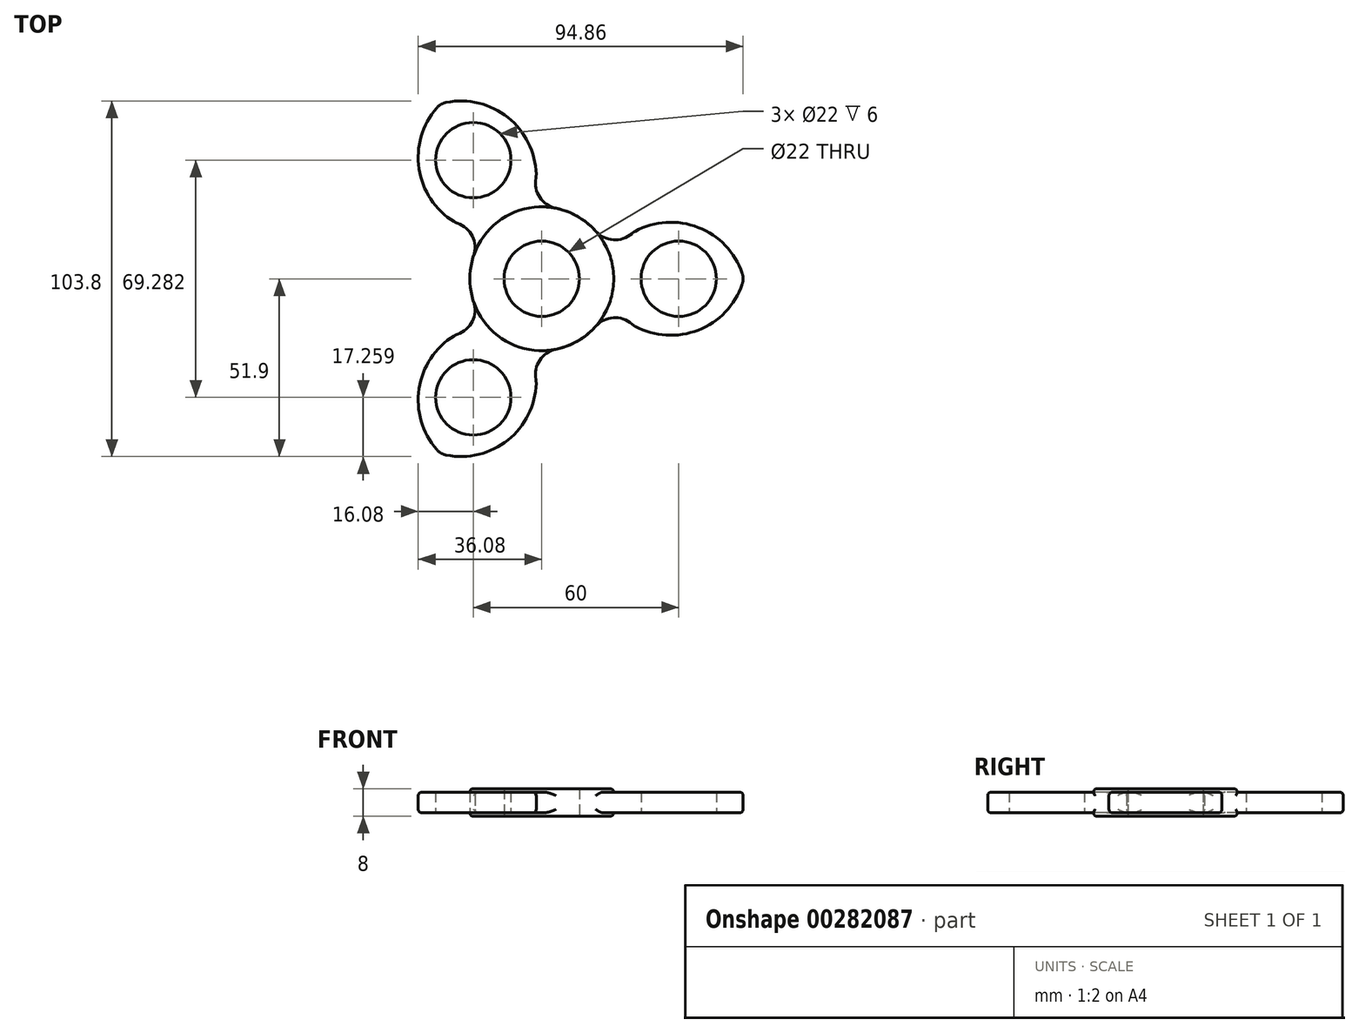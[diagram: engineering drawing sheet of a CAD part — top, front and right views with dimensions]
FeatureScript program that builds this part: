
annotation { "Feature Type Name" : "Feature", "Feature Type Description" : "" }
export const myFeature = defineFeature(function(context is Context, id is Id, definition is map)
    precondition{}
    {
        {
            var Q0;
            Q0=qCreatedBy(makeId("Top.planeOp"),FACE);
            var sketch = newSketch(context, id + "F0", { "sketchPlane" : qUnion([Q0])});
            skCircle(sketch, "E0", {"center": v(0, 0) * mm, "radius": 11 * mm});
            skCircle(sketch, "E1", {"center": v(0, 0) * mm, "radius": 21 * mm});
            skCircle(sketch, "E2", {"center": v(40, 0) * mm, "radius": 11 * mm});
            skCircle(sketch, "E3", {"center": v(40, 0) * mm, "radius": 19 * mm});
            skCircle(sketch, "E4", {"center": v(21.37, 18.85) * mm, "radius": 7.5 * mm});
            skCircle(sketch, "E5", {"center": v(21.37, -18.85) * mm, "radius": 7.5 * mm});
            skLineSegment(sketch, "E6", {"start": v(0, 0) * mm, "end": v(82.02, 0) * mm, "construction": true});
            skArc(sketch, "E7", {"start": v(59, 0) * mm, "mid": v(46.18, 14.8) * mm, "end": v(26.65, 13.52) * mm});
            skArc(sketch, "E8", {"start": v(26.65, -13.52) * mm, "mid": v(46.18, -14.8) * mm, "end": v(59, 0) * mm});
            skSolve(sketch);
        }
        {
            var Q0;
            Q0=makeQuery(id+"F0.imprint","IMPRINT",FACE,{"disambiguationData":[TD([[makeQuery(id+"F0.imprint","IMPRINT",EDGE,{"derivedFrom":sQuery(id+"F0.wireOp",EDGE,"E0")}),-1.0]])]});
            extrude(context, id + "F1", {"entities" : qUnion([Q0]), "depth" : 8 * mm, "symmetric" : true});
        }
        {
            var Q0;
            {var subQ0=sQuery(id+"F0.wireOp",EDGE,"E4");var subQ1=sQuery(id+"F0.wireOp",EDGE,"E1");var subQ2=makeQuery(id+"F0.imprint","INTERSECT",VERTEX,{"derivedFrom":[subQ1,subQ0]});Q0=makeQuery(id+"F0.imprint","IMPRINT",FACE,{"disambiguationData":[TD([[makeQuery(id+"F0.imprint","IMPRINT",EDGE,{"disambiguationData":[TD([[subQ2,1.0]])],"derivedFrom":subQ1}),-1.0]])]});}
            var Q1;
            Q1=makeQuery(id+"F0.imprint","IMPRINT",FACE,{"disambiguationData":[TD([[makeQuery(id+"F0.imprint","IMPRINT",EDGE,{"derivedFrom":sQuery(id+"F0.wireOp",EDGE,"E2")}),-1.0]])]});
            var Q2;
            {var subQ0=sQuery(id+"F0.wireOp",EDGE,"E5");var subQ1=sQuery(id+"F0.wireOp",EDGE,"E1");var subQ2=makeQuery(id+"F0.imprint","INTERSECT",VERTEX,{"derivedFrom":[subQ1,subQ0]});Q2=makeQuery(id+"F0.imprint","IMPRINT",FACE,{"disambiguationData":[TD([[makeQuery(id+"F0.imprint","IMPRINT",EDGE,{"disambiguationData":[TD([[subQ2,-1.0]])],"derivedFrom":subQ1}),-1.0]])]});}
            extrude(context, id + "F2", {"entities" : qUnion([Q0, Q1, Q2]), "operationType" : NewBodyOperationType.ADD, "depth" : 6 * mm, "symmetric" : true});
        }
        {
            var Q0;
            Q0=makeQuery(id+"F2.opExtrude","SWEPT_EDGE",EDGE,{"disambiguationData":[OSD([sQuery(id+"F0.wireOp",EDGE,"E3"),sQuery(id+"F0.wireOp",EDGE,"E7"),sQuery(id+"F0.wireOp",EDGE,"E8")])]});
            var Q1;
            Q1=makeQuery(id+"F2.opExtrude","SWEPT_EDGE",EDGE,{"disambiguationData":[OSD([sQuery(id+"F0.wireOp",EDGE,"E3"),sQuery(id+"F0.wireOp",EDGE,"E5"),sQuery(id+"F0.wireOp",EDGE,"E8")])]});
            var Q2;
            Q2=makeQuery(id+"F2.opExtrude","CAP_EDGE",EDGE,{"disambiguationData":[OSD([sQuery(id+"F0.wireOp",EDGE,"E1")])],"isStart":false});
            var Q3;
            Q3=makeQuery(id+"F2.opExtrude","CAP_EDGE",EDGE,{"disambiguationData":[OSD([sQuery(id+"F0.wireOp",EDGE,"E1")])],"isStart":true});
            var Q4;
            Q4=makeQuery(id+"F2.opExtrude","SWEPT_EDGE",EDGE,{"disambiguationData":[OSD([sQuery(id+"F0.wireOp",EDGE,"E3"),sQuery(id+"F0.wireOp",EDGE,"E4"),sQuery(id+"F0.wireOp",EDGE,"E7")])]});
            fillet(context, id + "F3", {"entities" : qUnion([Q0, Q1, Q2, Q3, Q4]), "radius" : 5 * mm, "tangentPropagation" : true, "allowEdgeOverflow" : false});
        }
        {
            var Q0;
            Q0=makeQuery(id+"F1.opExtrude","CAP_EDGE",EDGE,{"disambiguationData":[OSD([sQuery(id+"F0.wireOp",EDGE,"E1")])],"isStart":false});
            var Q1;
            Q1=makeQuery(id+"F1.opExtrude","CAP_EDGE",EDGE,{"disambiguationData":[OSD([sQuery(id+"F0.wireOp",EDGE,"E1")])],"isStart":true});
            var Q2;
            Q2=makeQuery(id+"F2.opExtrude","SWEPT_FACE",FACE,{"disambiguationData":[OSD([sQuery(id+"F0.wireOp",EDGE,"E8")])]});
            fillet(context, id + "F4", {"entities" : qUnion([Q0, Q1, Q2]), "radius" : 1 * mm, "tangentPropagation" : true, "allowEdgeOverflow" : false});
        }
        {
            var Q0;
            Q0=makeQuery(id+"F1.opExtrude","SWEPT_BODY",BODY,{"disambiguationData":[OSD([sQuery(id+"F0.wireOp",EDGE,"E0"),sQuery(id+"F0.wireOp",EDGE,"E1"),sQuery(id+"F0.wireOp",EDGE,"E2"),sQuery(id+"F0.wireOp",EDGE,"E4"),sQuery(id+"F0.wireOp",EDGE,"E5"),sQuery(id+"F0.wireOp",EDGE,"E7"),sQuery(id+"F0.wireOp",EDGE,"E8")])]});
            var Q1;
            Q1=makeQuery(id+"F1.opExtrude","SWEPT_FACE",FACE,{"disambiguationData":[OSD([sQuery(id+"F0.wireOp",EDGE,"E0")])]});
            circularPattern(context, id + "F5", {"operationType" : NewBodyOperationType.ADD, "entities" : qUnion([Q0]), "axis" : qUnion([Q1]), "angle" : 360 * degree, "instanceCount" : 3, "equalSpace" : true});
        }
    });
